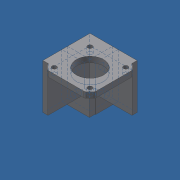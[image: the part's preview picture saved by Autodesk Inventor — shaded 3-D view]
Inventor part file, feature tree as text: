
AUTODESK INVENTOR PART (.ipt)
format: ipt  version: 2021 (Build 250183000, 183)  size: 225,280 bytes
history: native  units: mm
features: extrude x8, sketch x8, other x3, reference x1, projected_geometry x1
ambient origin geometry x8: Origin, YZ Plane, XZ Plane, XY Plane, X Axis, Y Axis, Z Axis, Center Point
bodies: Solid1 (feature_tree)
feature tree (21):
  extrude  "Extrusion1"  Depth=4.0mm
  extrude  "Extrusion3"  Depth=4.0mm
  extrude  "Extrusion4"  Depth=5.0mm TaperAngle=0.0deg
  extrude  "Extrusion9"  Depth=5.0mm
  extrude  "Extrusion7"  Depth=20.0mm
  extrude  "Extrusion10"  Depth=5.0mm TaperAngle=0.0deg
  extrude  "Extrusion11"  Depth=0.5mm
  extrude  "Extrusion12"  Depth=20.0mm TaperAngle=0.0deg
  sketch  "Sketch1"  dims[d0=24.0mm d1=4.0mm]
  reference  "Reference1"
  sketch  "Sketch3"  dims[d2=4.0mm d3=4.0mm]
  sketch  "Sketch4"  dims[d4=4.0mm d5=5.0mm d6=0.0mm]
  projected_geometry  "Projected Loop1"
  sketch  "Sketch7"  dims[d11=5.0mm d12=5.0mm]
  sketch  "Sketch11"  dims[d13=20.0mm d14=20.0mm]
  sketch  "Sketch12"  dims[d15=40.0mm d16=0.0mm d17=5.0mm d18=0.0mm]
  sketch  "Sketch13"  dims[d35=0.5mm d36=0.5mm]
  sketch  "Sketch14"  dims[d37=35.0mm d38=0.0mm d52=20.0mm d53=0.0mm d54=5.0mm d55=5.0mm d56=4.5mm d57=0.5mm d58=20.0mm d59=0.0mm d60=10.0mm d61=10.0mm d62=5.0mm d63=5.0mm d64=20.0mm d65=10.0mm d66=20.0mm d67=0.0mm d68=10.0mm d69=10.0mm d70=20.0mm d71=10.0mm d72=5.0mm d73=5.0mm d74=20.0mm d75=0.0mm]
  other  "<userpath>\OneDrive\Objet3D\3DPrinter\3DPrinterBeltCoreXY.iam"
  other  "3DPrinterBeltCoreXY.iam"
  other  "E3D Stepper Motor:1"
